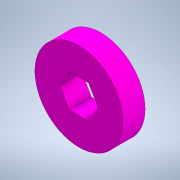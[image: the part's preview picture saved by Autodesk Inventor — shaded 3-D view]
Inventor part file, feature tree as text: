
AUTODESK INVENTOR PART (.ipt)
format: ipt  version: 2021.2 (Build 252289000, 289)  size: 107,008 bytes
history: native  units: in
note: dims shown in document units (in); Inventor stores cm internally (conversion verified against a paired STEP export)
features: extrude x1, sketch x1
ambient origin geometry x8: Origin, YZ Plane, XZ Plane, XY Plane, X Axis, Y Axis, Z Axis, Center Point
bodies: Solid1 (feature_tree)
feature tree (2):
  extrude  "Extrusion1"  Depth=0.25in
  sketch  "Sketch1"  dims[d0=0.375in d2=1.0in d3=0.2835in d4=0.25in d5=0.0in]
